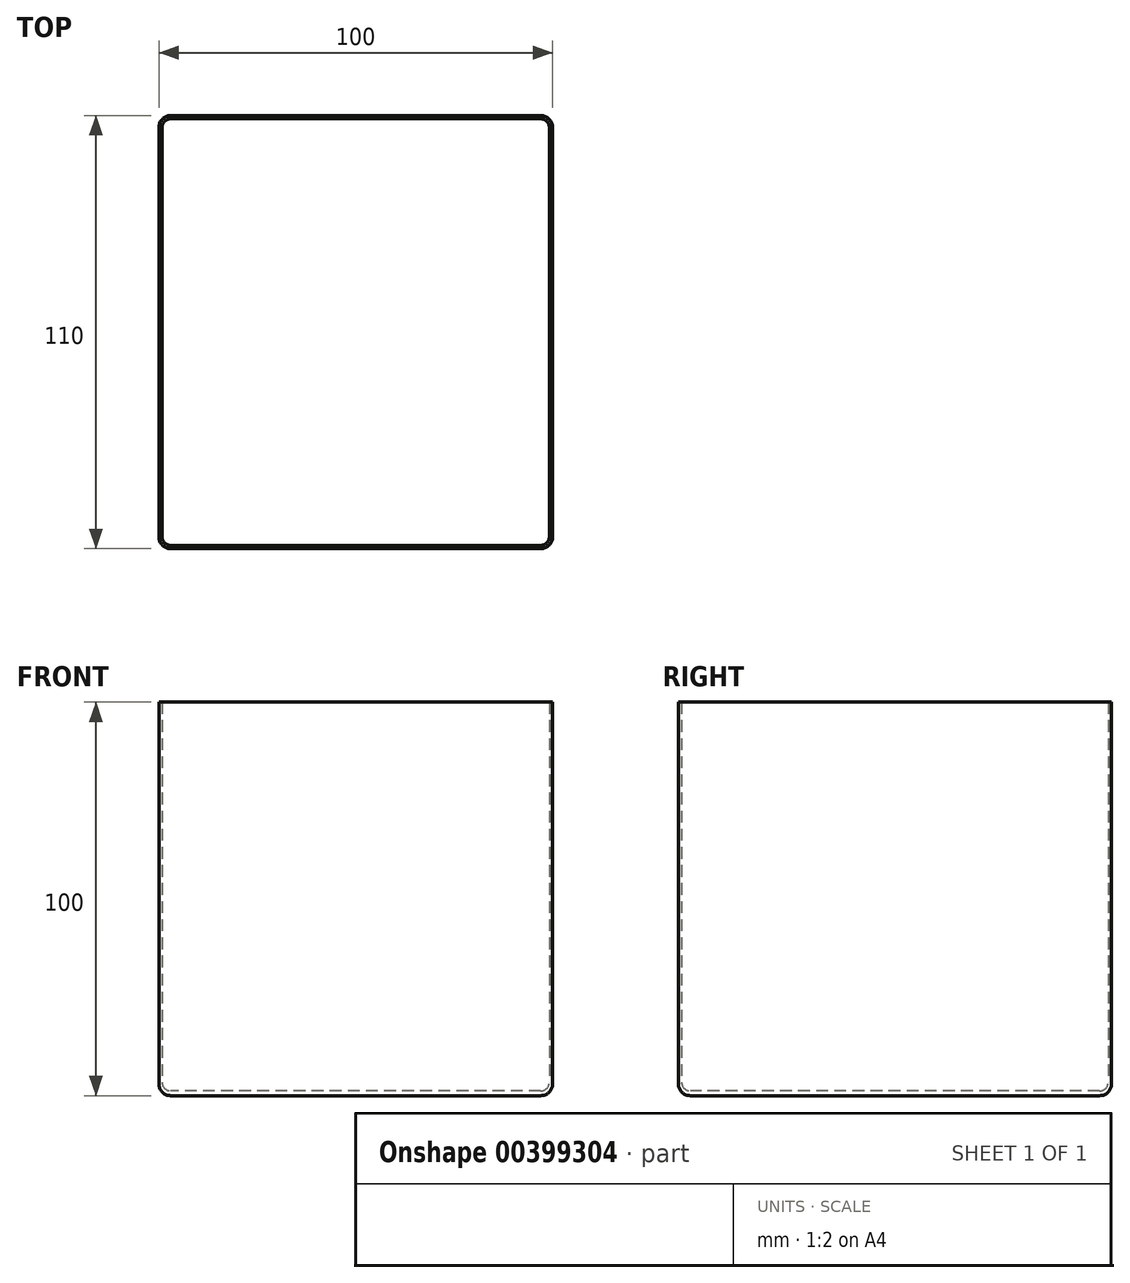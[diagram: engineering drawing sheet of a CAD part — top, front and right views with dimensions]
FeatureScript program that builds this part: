
annotation { "Feature Type Name" : "Feature", "Feature Type Description" : "" }
export const myFeature = defineFeature(function(context is Context, id is Id, definition is map)
    precondition{}
    {
        {
            var Q0;
            Q0=qCreatedBy(makeId("Top.planeOp"),FACE);
            var sketch = newSketch(context, id + "F0", { "sketchPlane" : qUnion([Q0])});
            skLineSegment(sketch, "E0.bottom", {"start": v(50, 55) * mm, "end": v(-50, 55) * mm});
            skLineSegment(sketch, "E0.top", {"start": v(50, -55) * mm, "end": v(-50, -55) * mm});
            skLineSegment(sketch, "E0.left", {"start": v(50, 55) * mm, "end": v(50, -55) * mm});
            skLineSegment(sketch, "E0.right", {"start": v(-50, 55) * mm, "end": v(-50, -55) * mm});
            skPoint(sketch, "E0.middle", {"position": v(0, 0) * mm});
            skLineSegment(sketch, "E1.bottom", {"start": v(49.2, 54.2) * mm, "end": v(-49.2, 54.2) * mm});
            skLineSegment(sketch, "E1.top", {"start": v(49.2, -54.2) * mm, "end": v(-49.2, -54.2) * mm});
            skLineSegment(sketch, "E1.left", {"start": v(49.2, 54.2) * mm, "end": v(49.2, -54.2) * mm});
            skLineSegment(sketch, "E1.right", {"start": v(-49.2, 54.2) * mm, "end": v(-49.2, -54.2) * mm});
            skSolve(sketch);
        }
        {
            var Q0;
            Q0=makeQuery(id+"F0.imprint","IMPRINT",FACE,{"disambiguationData":[TD([[makeQuery(id+"F0.imprint","IMPRINT",EDGE,{"derivedFrom":sQuery(id+"F0.wireOp",EDGE,"E1.bottom")}),1.0]])]});
            extrude(context, id + "F1", {"entities" : qUnion([Q0]), "depth" : 1.2 * mm});
        }
        {
            var Q0;
            Q0=makeQuery(id+"F0.imprint","IMPRINT",FACE,{"disambiguationData":[TD([[makeQuery(id+"F0.imprint","IMPRINT",EDGE,{"derivedFrom":sQuery(id+"F0.wireOp",EDGE,"E0.bottom")}),1.0]])]});
            extrude(context, id + "F2", {"entities" : qUnion([Q0]), "operationType" : NewBodyOperationType.ADD, "depth" : 100 * mm});
        }
        {
            var Q0;
            Q0=makeQuery(id+"F1.opExtrude","CAP_FACE",FACE,{"disambiguationData":[OSD([sQuery(id+"F0.wireOp",EDGE,"E1.bottom"),sQuery(id+"F0.wireOp",EDGE,"E1.top"),sQuery(id+"F0.wireOp",EDGE,"E1.left"),sQuery(id+"F0.wireOp",EDGE,"E1.right")])],"isStart":false});
            var Q1;
            Q1=makeQuery(id+"F2.opExtrude","SWEPT_EDGE",EDGE,{"disambiguationData":[OSD([sQuery(id+"F0.wireOp",EDGE,"E1.bottom"),sQuery(id+"F0.wireOp",EDGE,"E1.right")])]});
            var Q2;
            Q2=makeQuery(id+"F2.opExtrude","SWEPT_EDGE",EDGE,{"disambiguationData":[OSD([sQuery(id+"F0.wireOp",EDGE,"E1.top"),sQuery(id+"F0.wireOp",EDGE,"E1.right")])]});
            var Q3;
            Q3=makeQuery(id+"F2.opExtrude","SWEPT_EDGE",EDGE,{"disambiguationData":[OSD([sQuery(id+"F0.wireOp",EDGE,"E1.top"),sQuery(id+"F0.wireOp",EDGE,"E1.left")])]});
            var Q4;
            Q4=makeQuery(id+"F2.opExtrude","SWEPT_EDGE",EDGE,{"disambiguationData":[OSD([sQuery(id+"F0.wireOp",EDGE,"E1.bottom"),sQuery(id+"F0.wireOp",EDGE,"E1.left")])]});
            fillet(context, id + "F3", {"entities" : qUnion([Q0, Q1, Q2, Q3, Q4]), "radius" : 2.2 * mm, "tangentPropagation" : true, "allowEdgeOverflow" : false});
        }
        {
            var Q0;
            Q0=makeQuery(id+"F2.opExtrude","SWEPT_EDGE",EDGE,{"disambiguationData":[OSD([sQuery(id+"F0.wireOp",EDGE,"E0.bottom"),sQuery(id+"F0.wireOp",EDGE,"E0.left")])]});
            var Q1;
            {var subQ0=sQuery(id+"F0.wireOp",EDGE,"E1.right");var subQ1=sQuery(id+"F0.wireOp",EDGE,"E1.left");var subQ2=sQuery(id+"F0.wireOp",EDGE,"E1.top");var subQ3=sQuery(id+"F0.wireOp",EDGE,"E1.bottom");Q1=makeQuery(id+"F2.boolean.opBoolean","MERGE",FACE,{"derivedFrom":[makeQuery(id+"F1.opExtrude","CAP_FACE",FACE,{"disambiguationData":[OSD([subQ3,subQ2,subQ1,subQ0])],"isStart":true}),makeQuery(id+"F2.opExtrude","CAP_FACE",FACE,{"disambiguationData":[OSD([sQuery(id+"F0.wireOp",EDGE,"E0.bottom"),sQuery(id+"F0.wireOp",EDGE,"E0.top"),sQuery(id+"F0.wireOp",EDGE,"E0.left"),sQuery(id+"F0.wireOp",EDGE,"E0.right"),subQ3,subQ2,subQ1,subQ0])],"isStart":true})]});}
            var Q2;
            Q2=makeQuery(id+"F2.opExtrude","SWEPT_EDGE",EDGE,{"disambiguationData":[OSD([sQuery(id+"F0.wireOp",EDGE,"E0.bottom"),sQuery(id+"F0.wireOp",EDGE,"E0.right")])]});
            var Q3;
            Q3=makeQuery(id+"F2.opExtrude","SWEPT_EDGE",EDGE,{"disambiguationData":[OSD([sQuery(id+"F0.wireOp",EDGE,"E0.top"),sQuery(id+"F0.wireOp",EDGE,"E0.right")])]});
            var Q4;
            Q4=makeQuery(id+"F2.opExtrude","SWEPT_EDGE",EDGE,{"disambiguationData":[OSD([sQuery(id+"F0.wireOp",EDGE,"E0.top"),sQuery(id+"F0.wireOp",EDGE,"E0.left")])]});
            fillet(context, id + "F4", {"entities" : qUnion([Q0, Q1, Q2, Q3, Q4]), "radius" : 3 * mm, "tangentPropagation" : true, "allowEdgeOverflow" : false});
        }
    });
